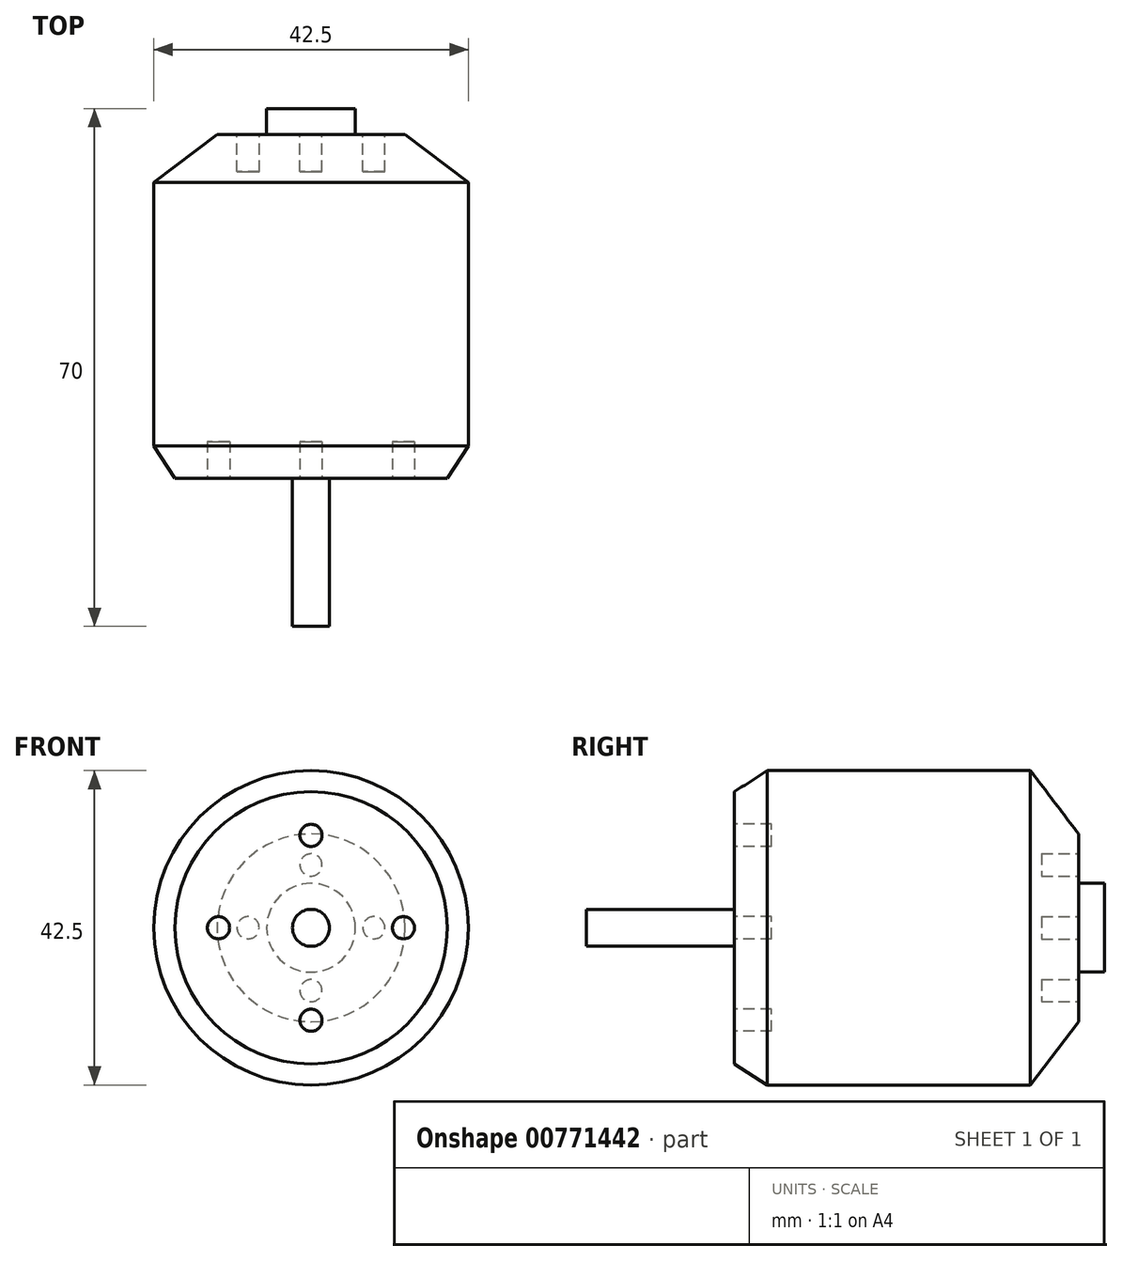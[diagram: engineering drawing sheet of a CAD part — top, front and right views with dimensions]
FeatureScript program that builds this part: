
annotation { "Feature Type Name" : "Feature", "Feature Type Description" : "" }
export const myFeature = defineFeature(function(context is Context, id is Id, definition is map)
    precondition{}
    {
        {
            var Q0;
            Q0=qCreatedBy(makeId("Right.planeOp"),FACE);
            var sketch = newSketch(context, id + "F0", { "sketchPlane" : qUnion([Q0])});
            skLineSegment(sketch, "E0", {"start": v(-20, 0) * mm, "end": v(-20, 2.5) * mm});
            skLineSegment(sketch, "E1", {"start": v(-20, 2.5) * mm, "end": v(0, 2.5) * mm});
            skLineSegment(sketch, "E2", {"start": v(0, 2.5) * mm, "end": v(0, 18.4) * mm});
            skLineSegment(sketch, "E3", {"start": v(0, 18.4) * mm, "end": v(4.4, 21.25) * mm});
            skLineSegment(sketch, "E4", {"start": v(4.4, 21.25) * mm, "end": v(40, 21.25) * mm});
            skLineSegment(sketch, "E5", {"start": v(40, 21.25) * mm, "end": v(46.5, 12.7) * mm});
            skLineSegment(sketch, "E6", {"start": v(46.5, 12.7) * mm, "end": v(46.5, 6) * mm});
            skLineSegment(sketch, "E7", {"start": v(46.5, 6) * mm, "end": v(50, 6) * mm});
            skLineSegment(sketch, "E8", {"start": v(50, 6) * mm, "end": v(50, 0) * mm});
            skLineSegment(sketch, "E9", {"start": v(50, 0) * mm, "end": v(-20, 0) * mm});
            skSolve(sketch);
        }
        {
            var Q0;
            Q0=makeQuery(id+"F0.imprint","IMPRINT",FACE,{"disambiguationData":[TD([[makeQuery(id+"F0.imprint","IMPRINT",EDGE,{"derivedFrom":sQuery(id+"F0.wireOp",EDGE,"E0")}),-1.0]])]});
            var Q1;
            Q1=sQuery(id+"F0.wireOp",EDGE,"E9");
            revolve(context, id + "F1", {"surfaceOperationType" : NewSurfaceOperationType.NEW, "entities" : qUnion([Q0]), "axis" : qUnion([Q1]), "revolveType" : RevolveType.FULL});
        }
        {
            var Q0;
            Q0=makeQuery(id+"F1.opRevolve","SWEPT_FACE",FACE,{"disambiguationData":[OSD([sQuery(id+"F0.wireOp",EDGE,"E2")])]});
            var sketch = newSketch(context, id + "F2", { "sketchPlane" : qUnion([Q0])});
            skCircle(sketch, "E10", {"center": v(12.5, 0) * mm, "radius": 1.5 * mm});
            skCircle(sketch, "E11.1.0", {"center": v(0, 12.5) * mm, "radius": 1.5 * mm});
            skCircle(sketch, "E11.2.0", {"center": v(-12.5, 0) * mm, "radius": 1.5 * mm});
            skCircle(sketch, "E11.3.0", {"center": v(0, -12.5) * mm, "radius": 1.5 * mm});
            skPoint(sketch, "E11.center", {"position": v(0, 0) * mm});
            skSolve(sketch);
        }
        {
            var Q0;
            Q0 = qSketchRegion(id + "F2", true);
            extrude(context, id + "F3", {"entities" : qUnion([Q0]), "operationType" : NewBodyOperationType.REMOVE, "oppositeDirection" : true, "depth" : 5 * mm, "offsetDistance" : 25 * mm});
        }
        {
            var Q0;
            Q0=makeQuery(id+"F1.opRevolve","SWEPT_FACE",FACE,{"disambiguationData":[OSD([sQuery(id+"F0.wireOp",EDGE,"E6")])]});
            var sketch = newSketch(context, id + "F4", { "sketchPlane" : qUnion([Q0])});
            skCircle(sketch, "E12", {"center": v(8.5, 0) * mm, "radius": 1.5 * mm});
            skCircle(sketch, "E13.1.0", {"center": v(0, 8.5) * mm, "radius": 1.5 * mm});
            skCircle(sketch, "E13.2.0", {"center": v(-8.5, 0) * mm, "radius": 1.5 * mm});
            skCircle(sketch, "E13.3.0", {"center": v(0, -8.5) * mm, "radius": 1.5 * mm});
            skPoint(sketch, "E13.center", {"position": v(0, 0) * mm});
            skSolve(sketch);
        }
        {
            var Q0;
            Q0 = qSketchRegion(id + "F4", true);
            extrude(context, id + "F5", {"entities" : qUnion([Q0]), "operationType" : NewBodyOperationType.REMOVE, "oppositeDirection" : true, "depth" : 5 * mm, "offsetDistance" : 25 * mm});
        }
    });
